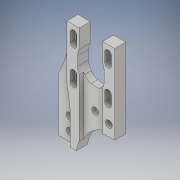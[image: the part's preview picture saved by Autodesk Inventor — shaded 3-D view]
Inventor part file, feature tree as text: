
AUTODESK INVENTOR PART (.ipt)
format: ipt  version: 2018 (Build 220112000, 112)  size: 372,736 bytes
history: native  units: in
note: dims shown in document units (in); Inventor stores cm internally (conversion verified against a paired STEP export)
features: extrude x12, sketch x12, projected_geometry x4, plane x2, fillet x1
ambient origin geometry x8: Origin, YZ Plane, XZ Plane, XY Plane, X Axis, Y Axis, Z Axis, Center Point
bodies: Solid1 (feature_tree)
feature tree (31):
  extrude  "Extrusion1"  Depth=1.6929in
  extrude  "Extrusion2"  Depth=0.4331in
  fillet  "Fillet1"  Radius=1.6535in
  extrude  "Extrusion3"  Depth=1.2205in
  extrude  "Extrusion4"  Depth=0.126in
  extrude  "Extrusion5"  Depth=0.315in
  plane  "Work Plane1"
  plane  "Work Plane2"
  extrude  "Extrusion9"  Depth=0.2362in TaperAngle=0.0deg
  sketch  "Sketch12"  dims[d15=0.315in d16=0.1575in d17=0.0in]
  extrude  "Extrusion13"  Depth=0.1575in TaperAngle=0.0deg
  extrude  "Extrusion14"  Depth=0.2362in
  extrude  "Extrusion15"  Depth=0.9449in
  extrude  "Extrusion16"  Depth=0.315in
  extrude  "Extrusion17"  Depth=0.2165in
  extrude  "Extrusion18"  Depth=0.3937in
  sketch  "Sketch1"  dims[d0=3.8189in d1=1.6929in]
  sketch  "Sketch2"  dims[d2=0.4331in d3=0.4331in d4=1.6535in]
  sketch  "Sketch3"  dims[d5=0.2362in d6=0.0in d7=1.2205in]
  projected_geometry  "Projected Loop1"
  sketch  "Sketch4"  dims[d8=1.2205in d9=0.126in]
  projected_geometry  "Projected Loop2"
  sketch  "Sketch5"  dims[d10=0.2756in d11=0.315in]
  projected_geometry  "Projected Loop3"
  sketch  "Sketch10"  dims[d12=0.315in d13=0.2362in d14=0.0in]
  projected_geometry  "Projected Loop4"
  sketch  "Sketch14"  dims[d18=0.2362in d20=0.2362in]
  sketch  "Sketch15"  dims[d21=0.1575in d22=0.0in d23=0.9449in]
  sketch  "Sketch16"  dims[d24=0.315in d25=0.6102in]
  sketch  "Sketch17"  dims[d26=0.0in d27=0.0in d43=0.2165in]
  sketch  "Sketch18"  dims[d44=0.1654in d47=0.3937in d50=0.2362in d51=0.0in d69=1.2992in d70=4.2606in d71=0.3937in d72=0.0in d73=0.1181in d74=1.063in d75=7.0866in d76=0.3937in d77=0.0in d78=0.2047in d79=0.2441in d80=0.2362in d81=0.0in d82=0.3937in d83=0.1654in d84=0.1654in d85=0.315in d86=0.4724in d87=0.2362in d88=0.0in d89=0.2441in d91=0.0787in d92=0.0in d93=0.7874in d94=0.3937in d95=0.0787in d96=0.0in]
